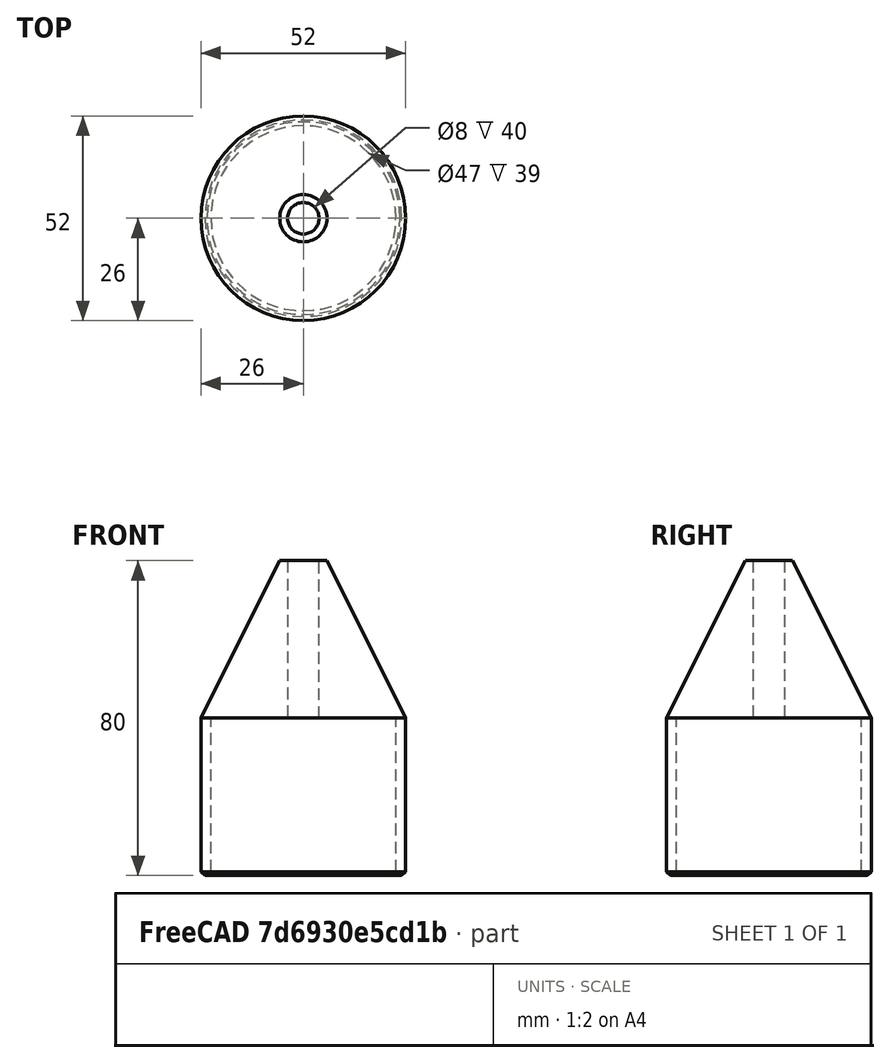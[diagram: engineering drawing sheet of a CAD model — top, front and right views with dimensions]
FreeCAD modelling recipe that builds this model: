
FCSTD DOCUMENT  (FreeCAD 1.0R39109 (Git))
Label: poraohjuri
License: All rights reserved
LicenseURL: https://en.wikipedia.org/wiki/All_rights_reserved
objects: PartDesign::Body×1, Part::FeaturePython×1, Part::Cone×1, Part::MultiFuse×1, Part::Cylinder×1, Part::Cut×1, Part::Chamfer×1
note: 7 computed .brp shape members not serialized (recipe doc carries the construction recipe); baked Part::Feature solids carry a one-line shape summary decoded from their .brp

FEATURE [PartDesign::Body] Body
  AllowCompound = false
  Origin = -> Origin
FEATURE [Part::FeaturePython] Tube  # WARN: FeaturePython — macro-defined, semantics opaque (R4)
  AttacherType = Attacher::AttachEngine3D
  Height = 40
  InnerRadius = 23.5
  OuterRadius = 26
FEATURE [Part::Cone] Cone
  Angle = 360
  AttacherType = Attacher::AttachEngine3D
  Height = 40
  Placement = pos=(0,0,40) rot=(0,0,1;0rad)
  Radius1 = 26
  Radius2 = 6
FEATURE [Part::MultiFuse] Fusion
  Shapes = -> [Cone,Tube]
FEATURE [Part::Cylinder] Cylinder
  Angle = 360
  AttacherType = Attacher::AttachEngine3D
  FirstAngle = 0
  Height = 40
  Placement = pos=(0,0,40) rot=(0,0,1;0rad)
  Radius = 4
  SecondAngle = 0
FEATURE [Part::Cut] Cut
  Base = -> Fusion
  Tool = -> Cylinder
FEATURE [Part::Chamfer] Chamfer
  Base = -> Cut
  EdgeLinks = -> Cut [Edge6,Edge9]
  Edges = 2 edges r=1: [Edge6,Edge9]
